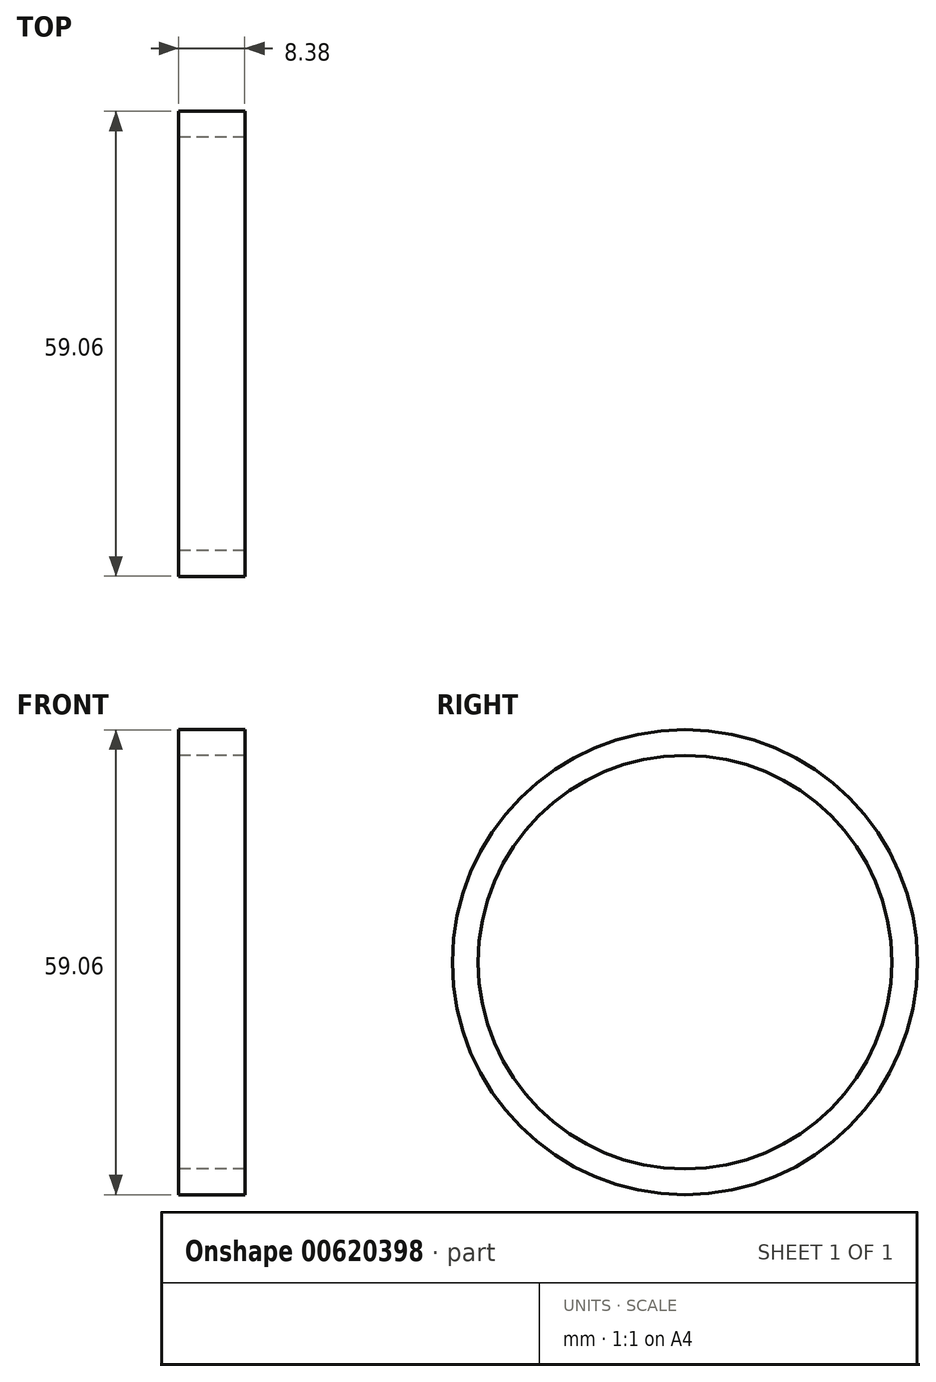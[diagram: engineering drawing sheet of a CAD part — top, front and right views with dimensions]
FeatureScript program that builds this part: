
annotation { "Feature Type Name" : "Feature", "Feature Type Description" : "" }
export const myFeature = defineFeature(function(context is Context, id is Id, definition is map)
    precondition{}
    {
        {
            var Q0;
            Q0=qCreatedBy(makeId("Right.planeOp"),FACE);
            var sketch = newSketch(context, id + "F0", { "sketchPlane" : qUnion([Q0])});
            skCircle(sketch, "E0", {"center": v(0, 0) * mm, "radius": 29.53 * mm});
            skCircle(sketch, "E1", {"center": v(0, 0) * mm, "radius": 26.28 * mm});
            skSolve(sketch);
        }
        {
            var Q0;
            Q0 = qSketchRegion(id + "F0", true);
            extrude(context, id + "F1", {"entities" : qUnion([Q0]), "depth" : 8.38 * mm, "offsetDistance" : 25.4 * mm});
        }
    });
